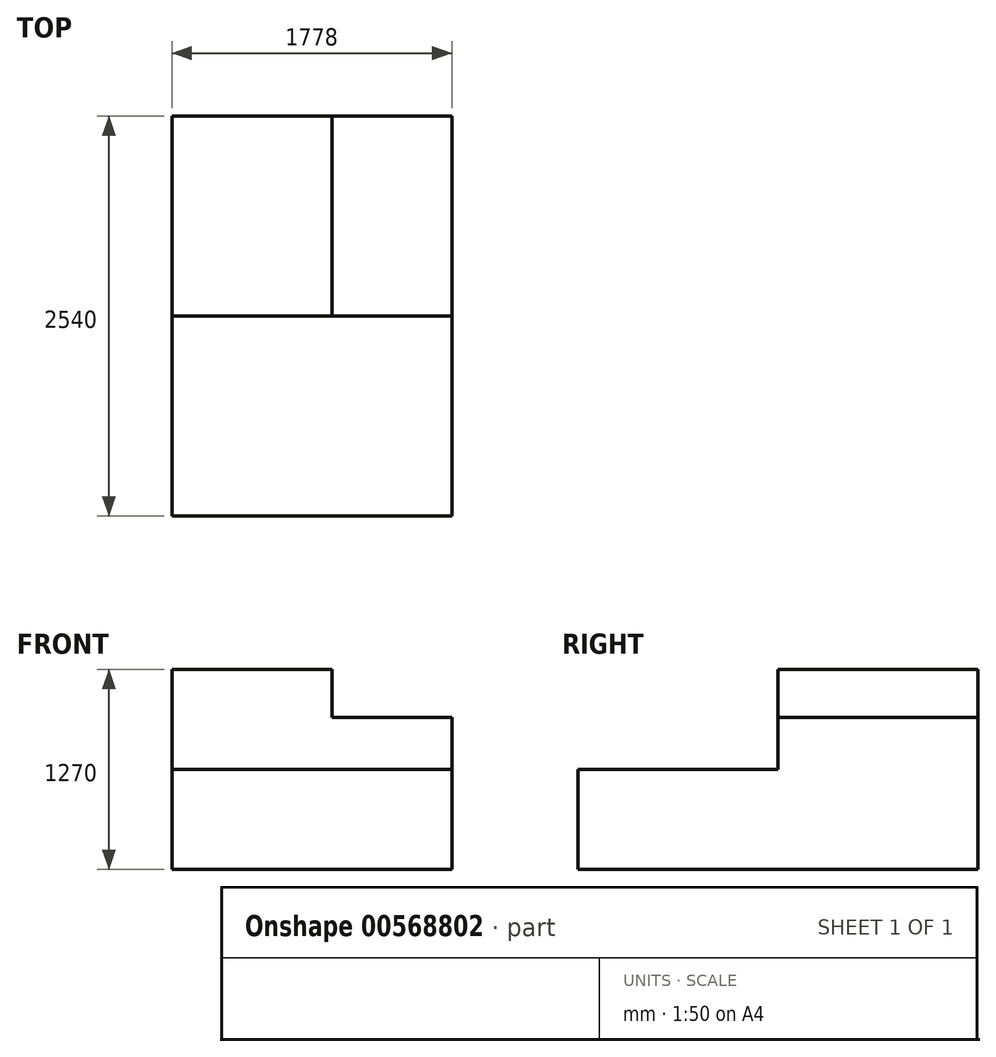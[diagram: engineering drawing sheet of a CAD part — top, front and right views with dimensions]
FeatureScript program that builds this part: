
annotation { "Feature Type Name" : "Feature", "Feature Type Description" : "" }
export const myFeature = defineFeature(function(context is Context, id is Id, definition is map)
    precondition{}
    {
        {
            var Q0;
            Q0=qCreatedBy(makeId("Right.planeOp"),FACE);
            var sketch = newSketch(context, id + "F0", { "sketchPlane" : qUnion([Q0])});
            skLineSegment(sketch, "E0", {"start": v(0, 0) * mm, "end": v(2540, 0) * mm});
            skLineSegment(sketch, "E1", {"start": v(2540, 0) * mm, "end": v(2540, 1270) * mm});
            skLineSegment(sketch, "E2", {"start": v(2540, 1270) * mm, "end": v(1270, 1270) * mm});
            skLineSegment(sketch, "E3", {"start": v(1270, 1270) * mm, "end": v(1270, 635) * mm});
            skLineSegment(sketch, "E4", {"start": v(1270, 635) * mm, "end": v(0, 635) * mm});
            skLineSegment(sketch, "E5", {"start": v(0, 635) * mm, "end": v(0, 0) * mm});
            skSolve(sketch);
        }
        {
            var Q0;
            Q0=makeQuery(id+"F0.imprint","IMPRINT",FACE,{"disambiguationData":[TD([[makeQuery(id+"F0.imprint","IMPRINT",EDGE,{"derivedFrom":sQuery(id+"F0.wireOp",EDGE,"E0")}),1.0]])]});
            extrude(context, id + "F1", {"entities" : qUnion([Q0]), "depth" : 1778 * mm, "offsetDistance" : 25.4 * mm});
        }
        {
            var Q0;
            Q0=makeQuery(id+"F1.opExtrude","CAP_FACE",FACE,{"disambiguationData":[OSD([sQuery(id+"F0.wireOp",EDGE,"E0"),sQuery(id+"F0.wireOp",EDGE,"E1"),sQuery(id+"F0.wireOp",EDGE,"E2"),sQuery(id+"F0.wireOp",EDGE,"E3"),sQuery(id+"F0.wireOp",EDGE,"E4"),sQuery(id+"F0.wireOp",EDGE,"E5")])],"isStart":false});
            var sketch = newSketch(context, id + "F2", { "sketchPlane" : qUnion([Q0])});
            skLineSegment(sketch, "E6", {"start": v(1270, 965.2) * mm, "end": v(2540, 965.2) * mm});
            skSolve(sketch);
        }
        {
            var Q0;
            {var subQ0=sQuery(id+"F2.wireOp",EDGE,"E6");Q0=makeQuery(id+"F2.imprint","IMPRINT",FACE,{"disambiguationData":[TD([[makeQuery(id+"F2.imprint","IMPRINT",EDGE,{"derivedFrom":subQ0}),1.0]])]});}
            extrude(context, id + "F3", {"entities" : qUnion([Q0]), "operationType" : NewBodyOperationType.REMOVE, "oppositeDirection" : true, "depth" : 762 * mm, "offsetDistance" : 25.4 * mm});
        }
    });
